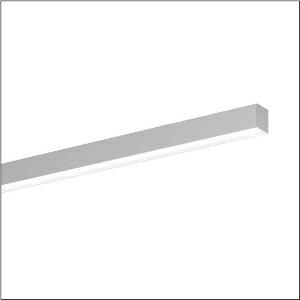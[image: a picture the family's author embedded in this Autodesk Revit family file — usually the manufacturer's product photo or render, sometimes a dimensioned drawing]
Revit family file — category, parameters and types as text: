
# Revit family: silica_r__21_51mx23tctas_d824
name_source: partatom
category: Lighting Fixtures
units: mm (PartAtom-declared; Revit-internal decimal feet)

## family parameters
Cut with Voids When Loaded = No
Host = Face
Light Source = No
Part Type = Normal
Room Calculation Point = No
Round Connector Dimension = Use Diameter
Shared = No

## types (1)
- --- (1 x LED, 8070 lm, 81.1 W, 6500K)
    Apparent Load = 81 VA
    CIE Flux Codes = 78 96 99 100 100
    Color Rendering = 80
    Color Temperature = 6500K
    Default Elevation = 1800 mm
    Description = Silica® 21, office luminaire, primary optical cover: prismatic diffuser, of PMMA, CAT 2 (L<= 3000cd/m²), light emission: direct distribution, primary light characteristic: symmetric, installation type: surface-mounted, LED, rated luminous flux: 8.070lm, luminous efficacy: 95lm/W, light colour: 8tw, colour temperature: 2700..6500K, control gear: ECG DALI, with terminal, 3+2-pole, max. 2.5mm², mains connection: 220..240V, AC, 50/60Hz, rated input power: 85.1W, luminaire housing, of aluminium, metallic grey (RAL 9006), length: 3.004mm, width: 53mm, height: 53mm, protection rating (complete): IP20, insulation class (complete): insulation class I (protective earthing), certification: CE, permissible operating ambient temperature: 0..+35°C, standard: EN 50419, packaging unit: 1 piece
    Height = 0 mm  [stored 0 ft]
    Lamp = 1 x LED
    Lamp Light Flux = 8070 lm
    Lamp Power = 81.1 W
    Lamp count = 1
    Length = 3004 mm
    Luminous efficacy = 100 lm/W
    Manufacturer = Siteco
    ModVariant = No
    Model = 51MX23TCTAS
    Mounting Place = Ceiling
    Mounting Type = Recessed
    Number of Poles = 1
    OnlyDefault = Yes
    Power Factor = 1
    Product Name = Silica® 21
    Product group = office luminaire | ceiling recessed
    ProductGroupID = 400
    Protection Class = Protection class I
    Protection Degree = IP 20
    RLX_Detail_Level = 1
    RLX_Emergency_Light_Flux = 0 lm
    RLX_Emergency_Type = 0
    RLX_Emergency_Type_DB = No
    RlxData = <blob elided: 17861 chars, md5=1dadc3fa>
    Socket = socket
    Standby Power = 0 W
    System Light Flux = 8070 lm
    System Power = 81 W
    Type Comments = individual setting
    Type Image = l_1335933.jpg
    URL = http://relux.com
    VarID = @adj_109591
    Voltage = 0 V
    Weight = 0.00 kg
    Width = 53 mm

note: [stored X ft] marks values corroborated as IEEE doubles in the binary element streams (Revit-internal decimal feet)

## geometry (parser evidence)
native form markers: Blend x4, Sweep x11
no freeform markers — native parametric forms only
